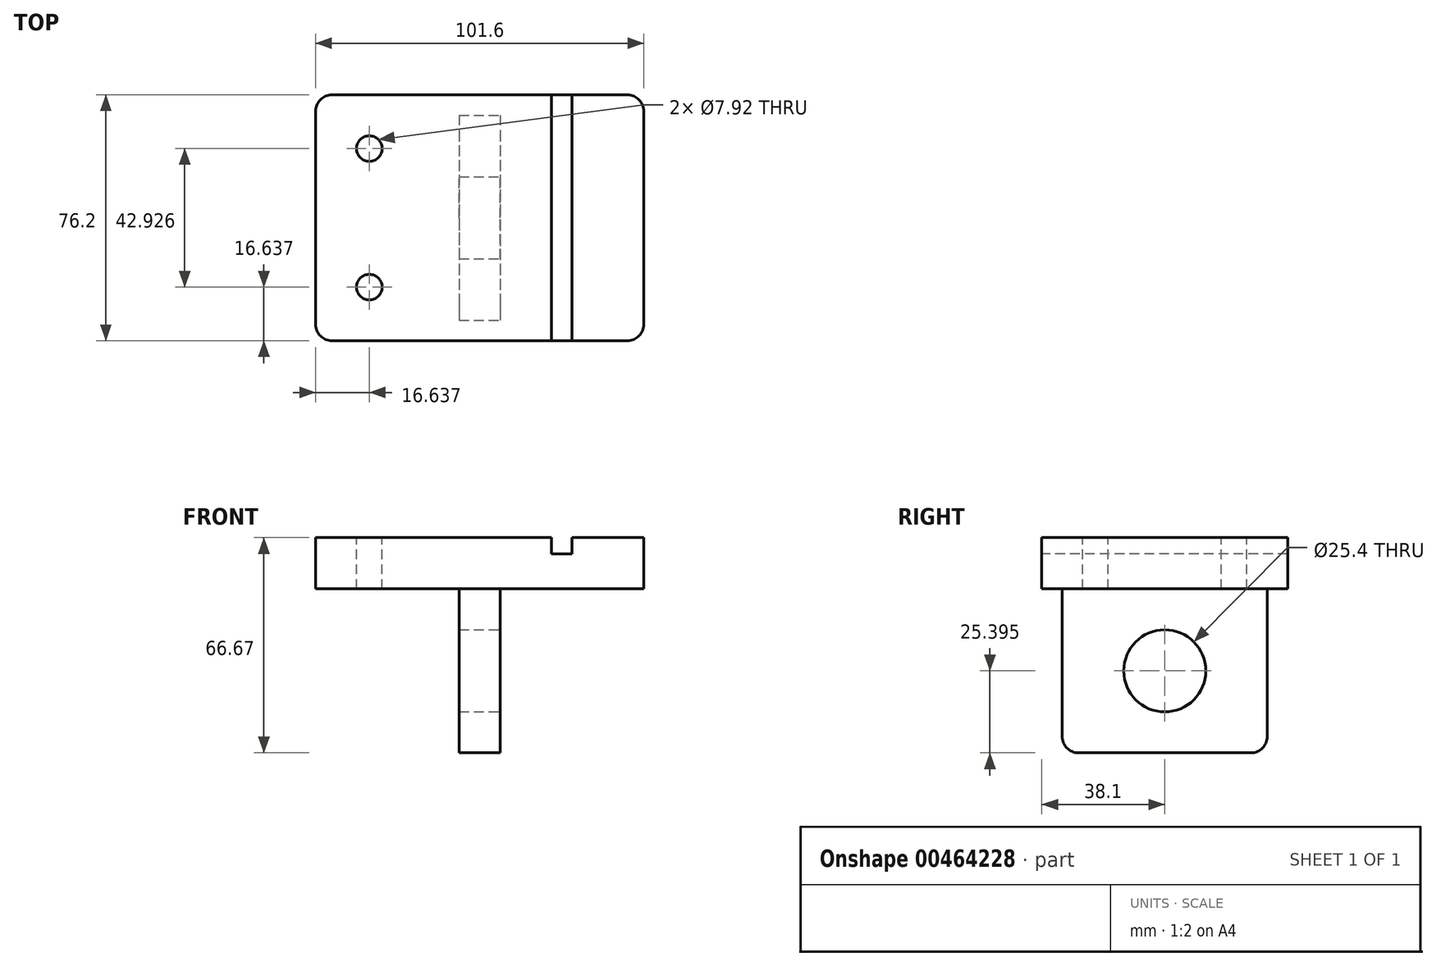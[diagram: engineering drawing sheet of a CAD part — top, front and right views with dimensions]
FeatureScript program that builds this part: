
annotation { "Feature Type Name" : "Feature", "Feature Type Description" : "" }
export const myFeature = defineFeature(function(context is Context, id is Id, definition is map)
    precondition{}
    {
        {
            var Q0;
            Q0=qCreatedBy(makeId("Top.planeOp"),FACE);
            var sketch = newSketch(context, id + "F0", { "sketchPlane" : qUnion([Q0])});
            skLineSegment(sketch, "E0.bottom", {"start": v(-50.8, 38.1) * mm, "end": v(50.8, 38.1) * mm});
            skLineSegment(sketch, "E0.top", {"start": v(-50.8, -38.1) * mm, "end": v(50.8, -38.1) * mm});
            skLineSegment(sketch, "E0.left", {"start": v(-50.8, 38.1) * mm, "end": v(-50.8, -38.1) * mm});
            skLineSegment(sketch, "E0.right", {"start": v(50.8, 38.1) * mm, "end": v(50.8, -38.1) * mm});
            skPoint(sketch, "E0.middle", {"position": v(0, 0) * mm});
            skLineSegment(sketch, "E1.bottom", {"start": v(-6.35, 31.75) * mm, "end": v(6.35, 31.75) * mm});
            skLineSegment(sketch, "E1.top", {"start": v(-6.35, -31.75) * mm, "end": v(6.35, -31.75) * mm});
            skLineSegment(sketch, "E1.left", {"start": v(-6.35, 31.75) * mm, "end": v(-6.35, -31.75) * mm});
            skLineSegment(sketch, "E1.right", {"start": v(6.35, 31.75) * mm, "end": v(6.35, -31.75) * mm});
            skCircle(sketch, "E2", {"center": v(-34.16, 21.46) * mm, "radius": 3.96 * mm});
            skCircle(sketch, "E3", {"center": v(-34.16, -21.46) * mm, "radius": 3.96 * mm});
            skSolve(sketch);
        }
        {
            var Q0;
            Q0 = qSketchRegion(id + "F0", true);
            extrude(context, id + "F1", {"entities" : qUnion([Q0]), "oppositeDirection" : true, "depth" : 15.88 * mm});
        }
        {
            var Q0;
            Q0=makeQuery(id+"F0.imprint","IMPRINT",FACE,{"disambiguationData":[TD([[makeQuery(id+"F0.imprint","IMPRINT",EDGE,{"derivedFrom":sQuery(id+"F0.wireOp",EDGE,"E1.bottom")}),-1.0]])]});
            extrude(context, id + "F2", {"entities" : qUnion([Q0]), "operationType" : NewBodyOperationType.ADD, "oppositeDirection" : true, "depth" : 66.67 * mm});
        }
        {
            var Q0;
            {var subQ0=sQuery(id+"F0.wireOp",EDGE,"E1.right");var subQ1=sQuery(id+"F0.wireOp",EDGE,"E1.left");var subQ2=sQuery(id+"F0.wireOp",EDGE,"E1.top");var subQ3=sQuery(id+"F0.wireOp",EDGE,"E1.bottom");Q0=makeQuery(id+"F2.boolean.opBoolean","MERGE",FACE,{"derivedFrom":[makeQuery(id+"F1.opExtrude","CAP_FACE",FACE,{"disambiguationData":[OSD([sQuery(id+"F0.wireOp",EDGE,"E0.bottom"),sQuery(id+"F0.wireOp",EDGE,"E0.top"),sQuery(id+"F0.wireOp",EDGE,"E0.left"),sQuery(id+"F0.wireOp",EDGE,"E0.right"),subQ3,subQ2,subQ1,subQ0,sQuery(id+"F0.wireOp",EDGE,"E2"),sQuery(id+"F0.wireOp",EDGE,"E3")])],"isStart":true}),makeQuery(id+"F2.opExtrude","CAP_FACE",FACE,{"disambiguationData":[OSD([subQ3,subQ2,subQ1,subQ0])],"isStart":true})]});}
            var sketch = newSketch(context, id + "F3", { "sketchPlane" : qUnion([Q0])});
            skLineSegment(sketch, "E4.bottom", {"start": v(22.23, 38.1) * mm, "end": v(28.57, 38.1) * mm});
            skLineSegment(sketch, "E4.top", {"start": v(22.23, -38.1) * mm, "end": v(28.57, -38.1) * mm});
            skLineSegment(sketch, "E4.left", {"start": v(22.23, 38.1) * mm, "end": v(22.23, -38.1) * mm});
            skLineSegment(sketch, "E4.right", {"start": v(28.57, 38.1) * mm, "end": v(28.57, -38.1) * mm});
            skPoint(sketch, "E4.middle", {"position": v(25.4, 0) * mm});
            skSolve(sketch);
        }
        {
            var Q0;
            Q0 = qSketchRegion(id + "F3", true);
            extrude(context, id + "F4", {"entities" : qUnion([Q0]), "operationType" : NewBodyOperationType.REMOVE, "oppositeDirection" : true, "depth" : 5.08 * mm});
        }
        {
            var Q0;
            Q0=makeQuery(id+"F2.opExtrude","SWEPT_FACE",FACE,{"disambiguationData":[OSD([sQuery(id+"F0.wireOp",EDGE,"E1.right")])]});
            var sketch = newSketch(context, id + "F5", { "sketchPlane" : qUnion([Q0])});
            skCircle(sketch, "E5", {"center": v(0, -41.28) * mm, "radius": 12.7 * mm});
            skSolve(sketch);
        }
        {
            var Q0;
            Q0 = qSketchRegion(id + "F5", true);
            extrude(context, id + "F6", {"entities" : qUnion([Q0]), "operationType" : NewBodyOperationType.REMOVE, "oppositeDirection" : true, "depth" : 25.4 * mm});
        }
        {
            var Q0;
            Q0=makeQuery(id+"F1.opExtrude","SWEPT_EDGE",EDGE,{"disambiguationData":[OSD([sQuery(id+"F0.wireOp",EDGE,"E0.top"),sQuery(id+"F0.wireOp",EDGE,"E0.right")])]});
            var Q1;
            Q1=makeQuery(id+"F1.opExtrude","SWEPT_EDGE",EDGE,{"disambiguationData":[OSD([sQuery(id+"F0.wireOp",EDGE,"E0.bottom"),sQuery(id+"F0.wireOp",EDGE,"E0.right")])]});
            var Q2;
            Q2=makeQuery(id+"F1.opExtrude","SWEPT_EDGE",EDGE,{"disambiguationData":[OSD([sQuery(id+"F0.wireOp",EDGE,"E0.bottom"),sQuery(id+"F0.wireOp",EDGE,"E0.left")])]});
            var Q3;
            Q3=makeQuery(id+"F1.opExtrude","SWEPT_EDGE",EDGE,{"disambiguationData":[OSD([sQuery(id+"F0.wireOp",EDGE,"E0.top"),sQuery(id+"F0.wireOp",EDGE,"E0.left")])]});
            var Q4;
            Q4=makeQuery(id+"F2.opExtrude","CAP_EDGE",EDGE,{"disambiguationData":[OSD([sQuery(id+"F0.wireOp",EDGE,"E1.top")])],"isStart":false});
            var Q5;
            Q5=makeQuery(id+"F2.opExtrude","CAP_EDGE",EDGE,{"disambiguationData":[OSD([sQuery(id+"F0.wireOp",EDGE,"E1.bottom")])],"isStart":false});
            var Q6;
            Q6=makeQuery(id+"F1.opExtrude","CAP_EDGE",EDGE,{"disambiguationData":[OSD([sQuery(id+"F0.wireOp",EDGE,"E1.top")])],"isStart":false});
            var Q7;
            Q7=makeQuery(id+"F1.opExtrude","CAP_EDGE",EDGE,{"disambiguationData":[OSD([sQuery(id+"F0.wireOp",EDGE,"E1.bottom")])],"isStart":false});
            fillet(context, id + "F7", {"entities" : qUnion([Q0, Q1, Q2, Q3, Q4, Q5, Q6, Q7]), "radius" : 5.08 * mm, "tangentPropagation" : true, "allowEdgeOverflow" : false});
        }
    });
